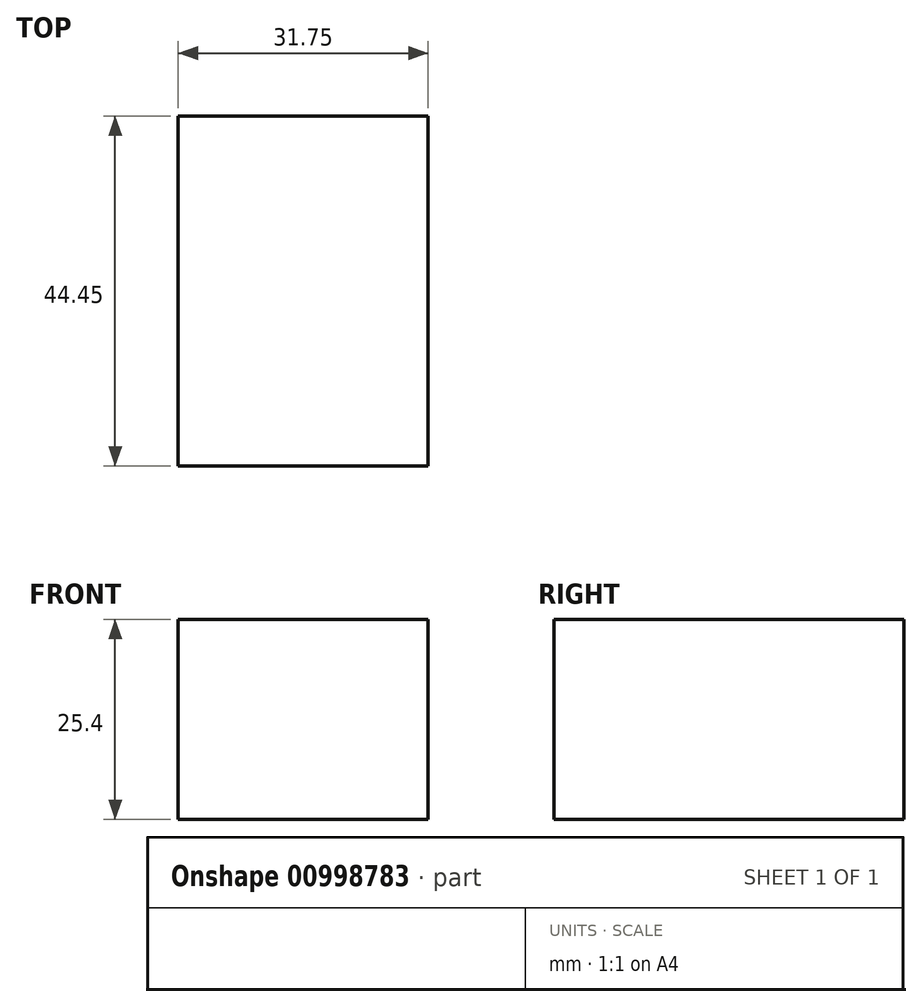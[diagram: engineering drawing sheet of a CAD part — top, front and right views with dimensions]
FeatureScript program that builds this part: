
annotation { "Feature Type Name" : "Feature", "Feature Type Description" : "" }
export const myFeature = defineFeature(function(context is Context, id is Id, definition is map)
    precondition{}
    {
        {
            var Q0;
            Q0=qCreatedBy(makeId("Front.planeOp"),FACE);
            var sketch = newSketch(context, id + "F0", { "sketchPlane" : qUnion([Q0])});
            skLineSegment(sketch, "E0.bottom", {"start": v(-9.82, 18.05) * mm, "end": v(21.93, 18.05) * mm});
            skLineSegment(sketch, "E0.top", {"start": v(-9.82, -7.35) * mm, "end": v(21.93, -7.35) * mm});
            skLineSegment(sketch, "E0.left", {"start": v(-9.82, 18.05) * mm, "end": v(-9.82, -7.35) * mm});
            skLineSegment(sketch, "E0.right", {"start": v(21.93, 18.05) * mm, "end": v(21.93, -7.35) * mm});
            skSolve(sketch);
        }
        {
            var Q0;
            Q0=makeQuery(id+"F0.imprint","IMPRINT",FACE,{"disambiguationData":[TD([[makeQuery(id+"F0.imprint","IMPRINT",EDGE,{"derivedFrom":sQuery(id+"F0.wireOp",EDGE,"E0.bottom")}),-1.0]])]});
            extrude(context, id + "F1", {"entities" : qUnion([Q0]), "depth" : 44.45 * mm, "offsetDistance" : 25.4 * mm});
        }
    });
